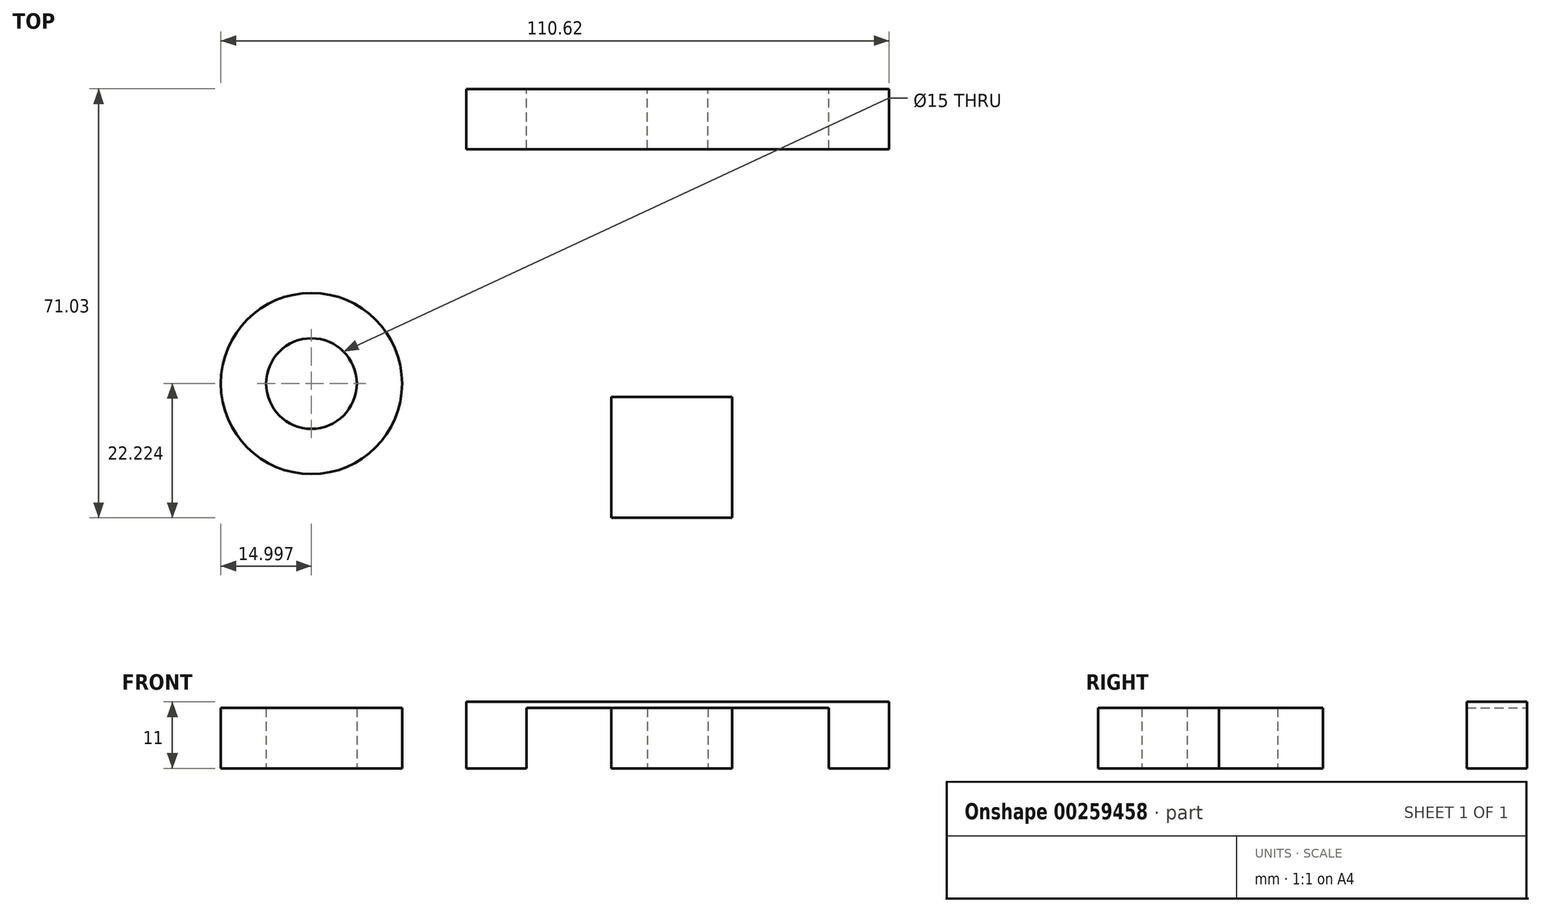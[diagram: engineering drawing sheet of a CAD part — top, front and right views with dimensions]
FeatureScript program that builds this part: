
annotation { "Feature Type Name" : "Feature", "Feature Type Description" : "" }
export const myFeature = defineFeature(function(context is Context, id is Id, definition is map)
    precondition{}
    {
        {
            var Q0;
            Q0=qCreatedBy(makeId("Top.planeOp"),FACE);
            var sketch = newSketch(context, id + "F0", { "sketchPlane" : qUnion([Q0])});
            skLineSegment(sketch, "E0.bottom", {"start": v(10, 10) * mm, "end": v(-10, 10) * mm});
            skLineSegment(sketch, "E0.top", {"start": v(10, -10) * mm, "end": v(-10, -10) * mm});
            skLineSegment(sketch, "E0.left", {"start": v(10, 10) * mm, "end": v(10, -10) * mm});
            skLineSegment(sketch, "E0.right", {"start": v(-10, 10) * mm, "end": v(-10, -10) * mm});
            skPoint(sketch, "E0.middle", {"position": v(0, 0) * mm});
            skSolve(sketch);
        }
        {
            var Q0;
            Q0 = qSketchRegion(id + "F0", true);
            extrude(context, id + "F1", {"entities" : qUnion([Q0]), "depth" : 10 * mm});
        }
        {
            var Q0;
            Q0=qCreatedBy(makeId("Top.planeOp"),FACE);
            var sketch = newSketch(context, id + "F2", { "sketchPlane" : qUnion([Q0])});
            skLineSegment(sketch, "E1.bottom", {"start": v(-24.02, 51.03) * mm, "end": v(-34.02, 51.03) * mm});
            skLineSegment(sketch, "E1.top", {"start": v(-24.02, 61.03) * mm, "end": v(-34.02, 61.03) * mm});
            skLineSegment(sketch, "E1.left", {"start": v(-24.02, 51.03) * mm, "end": v(-24.02, 61.03) * mm});
            skLineSegment(sketch, "E1.right", {"start": v(-34.02, 51.03) * mm, "end": v(-34.02, 61.03) * mm});
            skPoint(sketch, "E1.middle", {"position": v(-29.02, 56.03) * mm});
            skLineSegment(sketch, "E2.1.0.0", {"start": v(5.98, 61.03) * mm, "end": v(-4.02, 61.03) * mm});
            skLineSegment(sketch, "E2.1.0.1", {"start": v(5.98, 51.03) * mm, "end": v(5.98, 61.03) * mm});
            skLineSegment(sketch, "E2.1.0.2", {"start": v(5.98, 51.03) * mm, "end": v(-4.02, 51.03) * mm});
            skLineSegment(sketch, "E2.1.0.3", {"start": v(-4.02, 51.03) * mm, "end": v(-4.02, 61.03) * mm});
            skLineSegment(sketch, "E2.2.0.0", {"start": v(35.98, 61.03) * mm, "end": v(25.98, 61.03) * mm});
            skLineSegment(sketch, "E2.2.0.1", {"start": v(35.98, 51.03) * mm, "end": v(35.98, 61.03) * mm});
            skLineSegment(sketch, "E2.2.0.2", {"start": v(35.98, 51.03) * mm, "end": v(25.98, 51.03) * mm});
            skLineSegment(sketch, "E2.2.0.3", {"start": v(25.98, 51.03) * mm, "end": v(25.98, 61.03) * mm});
            skLineSegment(sketch, "E2.direction1", {"start": v(-34.02, 51.03) * mm, "end": v(-4.02, 51.03) * mm, "construction": true});
            skSolve(sketch);
        }
        {
            var Q0;
            Q0=makeQuery(id+"F2.imprint","IMPRINT",FACE,{"disambiguationData":[TD([[makeQuery(id+"F2.imprint","IMPRINT",EDGE,{"derivedFrom":sQuery(id+"F2.wireOp",EDGE,"E1.bottom")}),-1.0]])]});
            var Q1;
            Q1=makeQuery(id+"F2.imprint","IMPRINT",FACE,{"disambiguationData":[TD([[makeQuery(id+"F2.imprint","IMPRINT",EDGE,{"derivedFrom":sQuery(id+"F2.wireOp",EDGE,"E2.1.0.0")}),1.0]])]});
            var Q2;
            Q2=makeQuery(id+"F2.imprint","IMPRINT",FACE,{"disambiguationData":[TD([[makeQuery(id+"F2.imprint","IMPRINT",EDGE,{"derivedFrom":sQuery(id+"F2.wireOp",EDGE,"E2.2.0.0")}),1.0]])]});
            extrude(context, id + "F3", {"entities" : qUnion([Q0, Q1, Q2]), "depth" : 10 * mm});
        }
        {
            var Q0;
            Q0=makeQuery(id+"F3.opExtrude","CAP_FACE",FACE,{"disambiguationData":[OSD([sQuery(id+"F2.wireOp",EDGE,"E1.bottom"),sQuery(id+"F2.wireOp",EDGE,"E1.top"),sQuery(id+"F2.wireOp",EDGE,"E1.left"),sQuery(id+"F2.wireOp",EDGE,"E1.right")])],"isStart":false});
            var sketch = newSketch(context, id + "F4", { "sketchPlane" : qUnion([Q0])});
            skLineSegment(sketch, "E3.bottom", {"start": v(-34.02, 61.03) * mm, "end": v(35.98, 61.03) * mm});
            skLineSegment(sketch, "E3.top", {"start": v(-34.02, 51.03) * mm, "end": v(35.98, 51.03) * mm});
            skLineSegment(sketch, "E3.left", {"start": v(-34.02, 61.03) * mm, "end": v(-34.02, 51.03) * mm});
            skLineSegment(sketch, "E3.right", {"start": v(35.98, 61.03) * mm, "end": v(35.98, 51.03) * mm});
            skSolve(sketch);
        }
        {
            var Q0;
            Q0 = qSketchRegion(id + "F4", true);
            extrude(context, id + "F5", {"entities" : qUnion([Q0]), "operationType" : NewBodyOperationType.ADD, "depth" : 1 * mm});
        }
        {
            var Q0;
            Q0=qCreatedBy(makeId("Top.planeOp"),FACE);
            var sketch = newSketch(context, id + "F6", { "sketchPlane" : qUnion([Q0])});
            skCircle(sketch, "E4", {"center": v(-59.64, 12.22) * mm, "radius": 15 * mm});
            skCircle(sketch, "E5", {"center": v(-59.64, 12.22) * mm, "radius": 7.5 * mm});
            skSolve(sketch);
        }
        {
            var Q0;
            Q0 = qSketchRegion(id + "F6", true);
            extrude(context, id + "F7", {"entities" : qUnion([Q0]), "depth" : 10 * mm});
        }
    });
